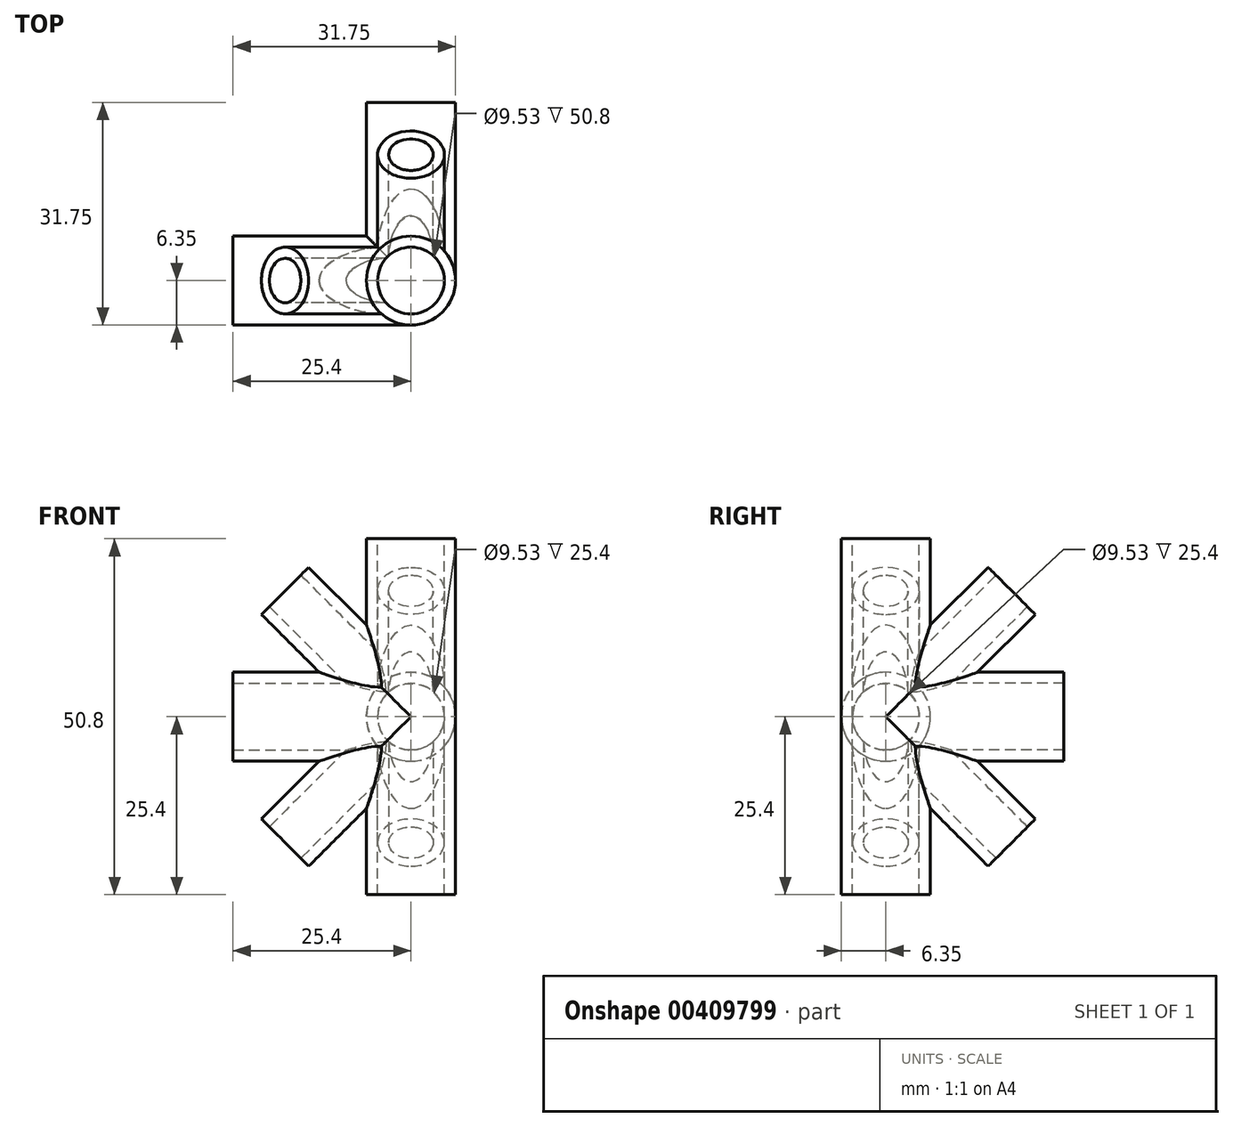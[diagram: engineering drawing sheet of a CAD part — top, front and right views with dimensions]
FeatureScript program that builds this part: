
annotation { "Feature Type Name" : "Feature", "Feature Type Description" : "" }
export const myFeature = defineFeature(function(context is Context, id is Id, definition is map)
    precondition{}
    {
        {
            var Q0;
            Q0=qCreatedBy(makeId("Top.planeOp"),FACE);
            var sketch = newSketch(context, id + "F0", { "sketchPlane" : qUnion([Q0])});
            skCircle(sketch, "E0", {"center": v(0, 0) * mm, "radius": 6.35 * mm});
            skSolve(sketch);
        }
        {
            var Q0;
            Q0=qSketchRegion(id+"F0",true);
            extrude(context, id + "F1", {"entities" : qUnion([Q0]), "depth" : 50.8 * mm, "symmetric" : true});
        }
        {
            var Q0;
            Q0=qCreatedBy(makeId("Right.planeOp"),FACE);
            var sketch = newSketch(context, id + "F2", { "sketchPlane" : qUnion([Q0])});
            skCircle(sketch, "E1", {"center": v(0, 0) * mm, "radius": 6.35 * mm});
            skSolve(sketch);
        }
        {
            var Q0;
            Q0=qSketchRegion(id+"F2",true);
            extrude(context, id + "F3", {"entities" : qUnion([Q0]), "operationType" : NewBodyOperationType.ADD, "oppositeDirection" : true, "depth" : 25.4 * mm});
        }
        {
            var Q0;
            Q0=qCreatedBy(makeId("Front.planeOp"),FACE);
            var sketch = newSketch(context, id + "F4", { "sketchPlane" : qUnion([Q0])});
            skCircle(sketch, "E2", {"center": v(0, 0) * mm, "radius": 6.35 * mm});
            skSolve(sketch);
        }
        {
            var Q0;
            Q0=qSketchRegion(id+"F4",true);
            extrude(context, id + "F5", {"entities" : qUnion([Q0]), "operationType" : NewBodyOperationType.ADD, "oppositeDirection" : true, "depth" : 25.4 * mm});
        }
        {
            var Q0;
            Q0=qCreatedBy(makeId("Top.planeOp"),FACE);
            var sketch = newSketch(context, id + "F6", { "sketchPlane" : qUnion([Q0])});
            skLineSegment(sketch, "E3", {"start": v(0, 0) * mm, "end": v(0, 25.4) * mm});
            skLineSegment(sketch, "E4", {"start": v(0, 0) * mm, "end": v(-25.4, 0) * mm});
            skSolve(sketch);
        }
        {
            var Q0;
            Q0=sQuery(id+"F6.wireOp",EDGE,"E4");
            cPlane(context, id + "F7", {"entities" : qUnion([Q0]), "cplaneType" : CPlaneType.LINE_ANGLE, "offset" : 25.4 * mm, "angle" : 45 * degree, "width" : 152.4 * mm, "height" : 152.4 * mm});
        }
        {
            var Q0;
            Q0=sQuery(id+"F6.wireOp",EDGE,"E4");
            cPlane(context, id + "F8", {"entities" : qUnion([Q0]), "cplaneType" : CPlaneType.LINE_ANGLE, "offset" : 25.4 * mm, "angle" : 135 * degree, "width" : 152.4 * mm, "height" : 152.4 * mm});
        }
        {
            var Q0;
            Q0=sQuery(id+"F6.wireOp",EDGE,"E3");
            cPlane(context, id + "F9", {"entities" : qUnion([Q0]), "cplaneType" : CPlaneType.LINE_ANGLE, "offset" : 25.4 * mm, "angle" : 45 * degree, "width" : 152.4 * mm, "height" : 152.4 * mm});
        }
        {
            var Q0;
            Q0=sQuery(id+"F6.wireOp",EDGE,"E3");
            cPlane(context, id + "F10", {"entities" : qUnion([Q0]), "cplaneType" : CPlaneType.LINE_ANGLE, "offset" : 25.4 * mm, "angle" : 135 * degree, "width" : 152.4 * mm, "height" : 152.4 * mm});
        }
        {
            var Q0;
            Q0=qCreatedBy(id+"F7.planeOp",FACE);
            var sketch = newSketch(context, id + "F11", { "sketchPlane" : qUnion([Q0])});
            skCircle(sketch, "E5", {"center": v(0, 0) * mm, "radius": 4.76 * mm});
            skSolve(sketch);
        }
        {
            var Q0;
            Q0=qSketchRegion(id+"F11",true);
            extrude(context, id + "F12", {"entities" : qUnion([Q0]), "operationType" : NewBodyOperationType.ADD, "oppositeDirection" : true, "depth" : 25.4 * mm});
        }
        {
            var Q0;
            Q0=qCreatedBy(id+"F8.planeOp",FACE);
            var sketch = newSketch(context, id + "F13", { "sketchPlane" : qUnion([Q0])});
            skCircle(sketch, "E6", {"center": v(0, 0) * mm, "radius": 4.76 * mm});
            skSolve(sketch);
        }
        {
            var Q0;
            Q0=qSketchRegion(id+"F13",true);
            extrude(context, id + "F14", {"entities" : qUnion([Q0]), "operationType" : NewBodyOperationType.ADD, "depth" : 25.4 * mm});
        }
        {
            var Q0;
            Q0=qCreatedBy(id+"F9.planeOp",FACE);
            var sketch = newSketch(context, id + "F15", { "sketchPlane" : qUnion([Q0])});
            skCircle(sketch, "E7", {"center": v(0, 0) * mm, "radius": 4.76 * mm});
            skSolve(sketch);
        }
        {
            var Q0;
            Q0=qSketchRegion(id+"F15",true);
            extrude(context, id + "F16", {"entities" : qUnion([Q0]), "operationType" : NewBodyOperationType.ADD, "oppositeDirection" : true, "depth" : 25.4 * mm});
        }
        {
            var Q0;
            Q0=qCreatedBy(id+"F10.planeOp",FACE);
            var sketch = newSketch(context, id + "F17", { "sketchPlane" : qUnion([Q0])});
            skCircle(sketch, "E8", {"center": v(0, 0) * mm, "radius": 4.76 * mm});
            skSolve(sketch);
        }
        {
            var Q0;
            Q0=qSketchRegion(id+"F17",true);
            extrude(context, id + "F18", {"entities" : qUnion([Q0]), "operationType" : NewBodyOperationType.ADD, "oppositeDirection" : true, "depth" : 25.4 * mm});
        }
        {
            var Q0;
            Q0=makeQuery(id+"F1.opExtrude","CAP_FACE",FACE,{"disambiguationData":[OSD([sQuery(id+"F0.wireOp",EDGE,"E0")])],"isStart":false});
            var sketch = newSketch(context, id + "F19", { "sketchPlane" : qUnion([Q0])});
            skCircle(sketch, "E9", {"center": v(0, 0) * mm, "radius": 4.76 * mm});
            skSolve(sketch);
        }
        {
            var Q0;
            Q0 = qSketchRegion(id + "F19", true);
            extrude(context, id + "F20", {"entities" : qUnion([Q0]), "operationType" : NewBodyOperationType.REMOVE, "endBound" : BoundingType.THROUGH_ALL, "oppositeDirection" : true, "depth" : 25.4 * mm});
        }
        {
            var Q0;
            Q0=qCreatedBy(makeId("Front.planeOp"),FACE);
            var sketch = newSketch(context, id + "F21", { "sketchPlane" : qUnion([Q0])});
            skCircle(sketch, "E10", {"center": v(0, 0) * mm, "radius": 4.76 * mm});
            skSolve(sketch);
        }
        {
            var Q0;
            Q0 = qSketchRegion(id + "F21", true);
            extrude(context, id + "F22", {"entities" : qUnion([Q0]), "operationType" : NewBodyOperationType.REMOVE, "endBound" : BoundingType.THROUGH_ALL, "oppositeDirection" : true, "depth" : 25.4 * mm});
        }
        {
            var Q0;
            Q0=qCreatedBy(makeId("Right.planeOp"),FACE);
            var sketch = newSketch(context, id + "F23", { "sketchPlane" : qUnion([Q0])});
            skCircle(sketch, "E11", {"center": v(0, 0) * mm, "radius": 4.76 * mm});
            skSolve(sketch);
        }
        {
            var Q0;
            Q0 = qSketchRegion(id + "F23", true);
            extrude(context, id + "F24", {"entities" : qUnion([Q0]), "operationType" : NewBodyOperationType.REMOVE, "endBound" : BoundingType.THROUGH_ALL, "oppositeDirection" : true, "depth" : 25.4 * mm});
        }
        {
            var Q0;
            Q0=makeQuery(id+"F18.opExtrude","CAP_FACE",FACE,{"disambiguationData":[OSD([sQuery(id+"F17.wireOp",EDGE,"E8")])],"isStart":false});
            var sketch = newSketch(context, id + "F25", { "sketchPlane" : qUnion([Q0])});
            skCircle(sketch, "E12", {"center": v(0, 0) * mm, "radius": 3.18 * mm});
            skSolve(sketch);
        }
        {
            var Q0;
            Q0 = qSketchRegion(id + "F25", true);
            extrude(context, id + "F26", {"entities" : qUnion([Q0]), "operationType" : NewBodyOperationType.REMOVE, "endBound" : BoundingType.UP_TO_NEXT, "oppositeDirection" : true, "depth" : 25.4 * mm});
        }
        {
            var Q0;
            Q0=makeQuery(id+"F14.opExtrude","CAP_FACE",FACE,{"disambiguationData":[OSD([sQuery(id+"F13.wireOp",EDGE,"E6")])],"isStart":false});
            var sketch = newSketch(context, id + "F27", { "sketchPlane" : qUnion([Q0])});
            skCircle(sketch, "E13", {"center": v(0, 0) * mm, "radius": 3.18 * mm});
            skSolve(sketch);
        }
        {
            var Q0;
            Q0 = qSketchRegion(id + "F27", true);
            extrude(context, id + "F28", {"entities" : qUnion([Q0]), "operationType" : NewBodyOperationType.REMOVE, "endBound" : BoundingType.UP_TO_NEXT, "oppositeDirection" : true, "depth" : 25.4 * mm});
        }
        {
            var Q0;
            Q0=makeQuery(id+"F16.opExtrude","CAP_FACE",FACE,{"disambiguationData":[OSD([sQuery(id+"F15.wireOp",EDGE,"E7")])],"isStart":false});
            var sketch = newSketch(context, id + "F29", { "sketchPlane" : qUnion([Q0])});
            skCircle(sketch, "E14", {"center": v(0, 0) * mm, "radius": 3.18 * mm});
            skSolve(sketch);
        }
        {
            var Q0;
            Q0 = qSketchRegion(id + "F29", true);
            extrude(context, id + "F30", {"entities" : qUnion([Q0]), "operationType" : NewBodyOperationType.REMOVE, "endBound" : BoundingType.UP_TO_NEXT, "oppositeDirection" : true, "depth" : 25.4 * mm});
        }
        {
            var Q0;
            Q0=makeQuery(id+"F12.opExtrude","CAP_FACE",FACE,{"disambiguationData":[OSD([sQuery(id+"F11.wireOp",EDGE,"E5")])],"isStart":false});
            var sketch = newSketch(context, id + "F31", { "sketchPlane" : qUnion([Q0])});
            skCircle(sketch, "E15", {"center": v(0, 0) * mm, "radius": 3.18 * mm});
            skSolve(sketch);
        }
        {
            var Q0;
            Q0 = qSketchRegion(id + "F31", true);
            extrude(context, id + "F32", {"entities" : qUnion([Q0]), "operationType" : NewBodyOperationType.REMOVE, "endBound" : BoundingType.UP_TO_NEXT, "oppositeDirection" : true, "depth" : 25.4 * mm});
        }
    });
